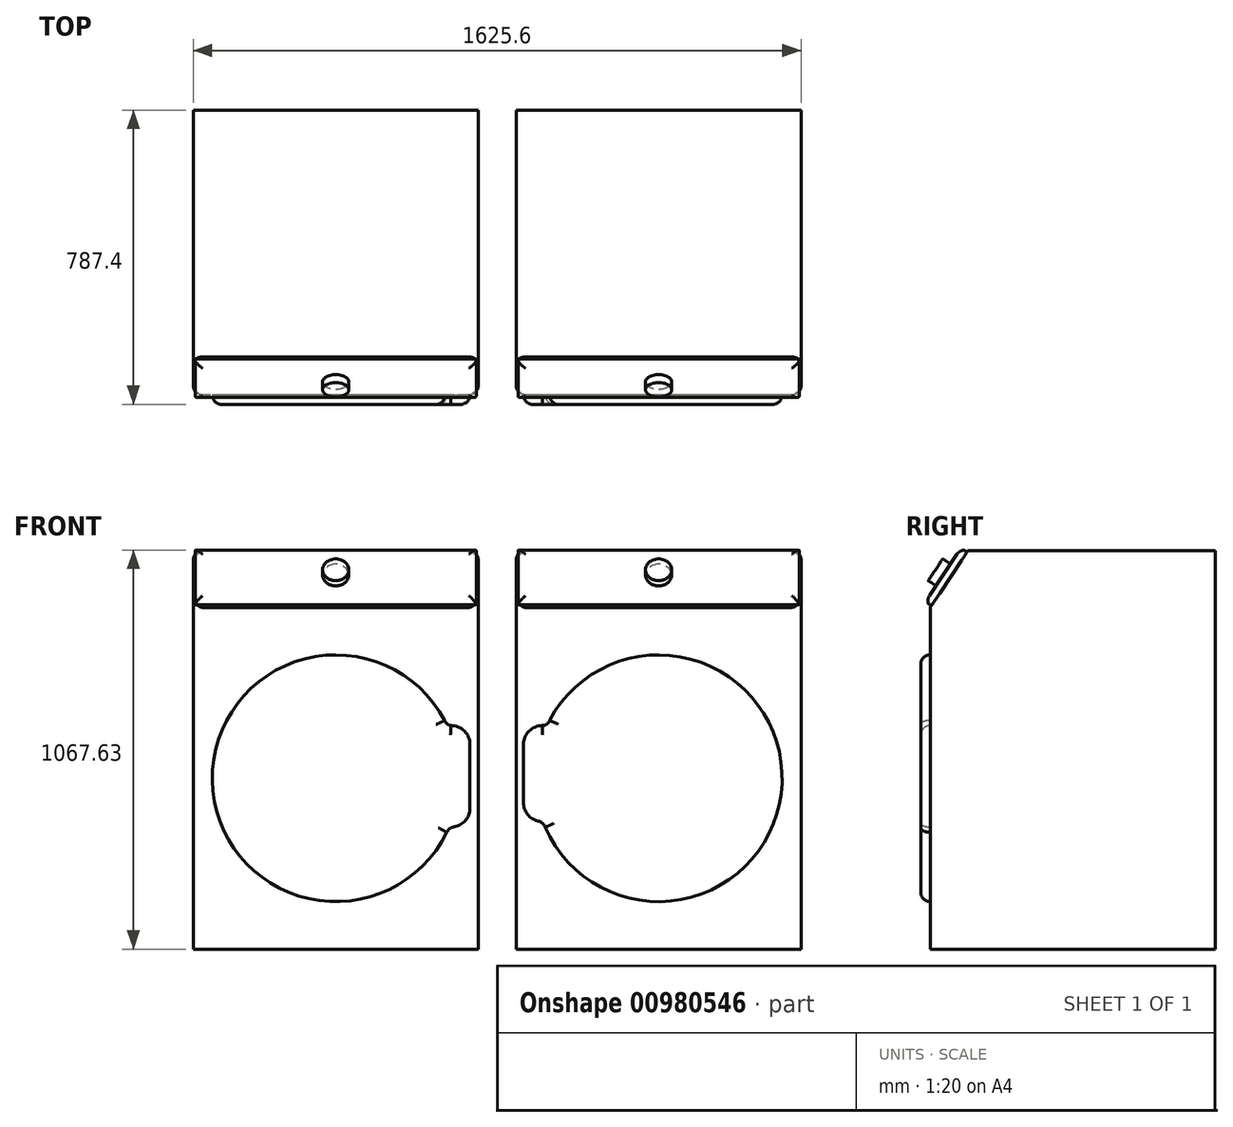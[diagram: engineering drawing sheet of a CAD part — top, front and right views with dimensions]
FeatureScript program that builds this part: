
annotation { "Feature Type Name" : "Feature", "Feature Type Description" : "" }
export const myFeature = defineFeature(function(context is Context, id is Id, definition is map)
    precondition{}
    {
        {
            var Q0;
            Q0=qCreatedBy(makeId("Top.planeOp"),FACE);
            var sketch = newSketch(context, id + "F0", { "sketchPlane" : qUnion([Q0])});
            skLineSegment(sketch, "E0.bottom", {"start": v(-50.8, 381) * mm, "end": v(-812.8, 381) * mm});
            skLineSegment(sketch, "E0.top", {"start": v(-50.8, -381) * mm, "end": v(-812.8, -381) * mm});
            skLineSegment(sketch, "E0.left", {"start": v(-50.8, 381) * mm, "end": v(-50.8, -381) * mm});
            skLineSegment(sketch, "E0.right", {"start": v(-812.8, 381) * mm, "end": v(-812.8, -381) * mm});
            skPoint(sketch, "E0.middle", {"position": v(-431.8, 0) * mm});
            skLineSegment(sketch, "E1.bottom", {"start": v(812.8, 381) * mm, "end": v(50.8, 381) * mm});
            skLineSegment(sketch, "E1.top", {"start": v(812.8, -381) * mm, "end": v(50.8, -381) * mm});
            skLineSegment(sketch, "E1.left", {"start": v(812.8, 381) * mm, "end": v(812.8, -381) * mm});
            skLineSegment(sketch, "E1.right", {"start": v(50.8, 381) * mm, "end": v(50.8, -381) * mm});
            skPoint(sketch, "E1.middle", {"position": v(431.8, 0) * mm});
            skLineSegment(sketch, "E2", {"start": v(-431.8, 0) * mm, "end": v(420.9, 0) * mm, "construction": true});
            skSolve(sketch);
        }
        {
            var Q0;
            Q0=makeQuery(id+"F0.imprint","IMPRINT",FACE,{"disambiguationData":[TD([[makeQuery(id+"F0.imprint","IMPRINT",EDGE,{"derivedFrom":sQuery(id+"F0.wireOp",EDGE,"E0.bottom")}),1.0]])]});
            var Q1;
            Q1=makeQuery(id+"F0.imprint","IMPRINT",FACE,{"disambiguationData":[TD([[makeQuery(id+"F0.imprint","IMPRINT",EDGE,{"derivedFrom":sQuery(id+"F0.wireOp",EDGE,"E1.bottom")}),1.0]])]});
            extrude(context, id + "F1", {"entities" : qUnion([Q0, Q1]), "depth" : 1066.8 * mm, "offsetDistance" : 25.4 * mm});
        }
        {
            var Q0;
            Q0=makeQuery(id+"F1.opExtrude","CAP_EDGE",EDGE,{"disambiguationData":[OSD([sQuery(id+"F0.wireOp",EDGE,"E0.top")])],"isStart":false});
            var Q1;
            Q1=makeQuery(id+"F1.opExtrude","CAP_EDGE",EDGE,{"disambiguationData":[OSD([sQuery(id+"F0.wireOp",EDGE,"E1.top")])],"isStart":false});
            chamfer(context, id + "F2", {"entities" : qUnion([Q0, Q1]), "chamferType" : ChamferType.TWO_OFFSETS, "width1" : 152.4 * mm, "oppositeDirection" : false, "width2" : 101.6 * mm, "tangentPropagation" : true});
        }
        {
            var Q0;
            Q0=makeQuery(id+"F2.opChamfer","BLEND_FACE",FACE,{"disambiguationData":[OSD([sQuery(id+"F0.wireOp",EDGE,"E0.top")])]});
            var Q1;
            Q1=makeQuery(id+"F2.opChamfer","BLEND_FACE",FACE,{"disambiguationData":[OSD([sQuery(id+"F0.wireOp",EDGE,"E1.top")])]});
            extrude(context, id + "F3", {"entities" : qUnion([Q0, Q1]), "depth" : 19.05 * mm, "offsetDistance" : 25.4 * mm});
        }
        {
            var Q0;
            Q0=makeQuery(id+"F1.opExtrude","SWEPT_FACE",FACE,{"disambiguationData":[OSD([sQuery(id+"F0.wireOp",EDGE,"E0.top")])]});
            var sketch = newSketch(context, id + "F4", { "sketchPlane" : qUnion([Q0])});
            skLineSegment(sketch, "E3", {"start": v(-50.8, 457.2) * mm, "end": v(-812.8, 457.2) * mm, "construction": true});
            skArc(sketch, "E4", {"start": v(-140.06, 611.86) * mm, "mid": v(-761.95, 451.64) * mm, "end": v(-135.01, 312.46) * mm});
            skLineSegment(sketch, "E5", {"start": v(-50.8, 457.2) * mm, "end": v(50.8, 457.2) * mm, "construction": true});
            skLineSegment(sketch, "E6", {"start": v(50.8, 457.2) * mm, "end": v(812.8, 457.2) * mm, "construction": true});
            skArc(sketch, "E7", {"start": v(128.77, 326.03) * mm, "mid": v(761.74, 444.17) * mm, "end": v(140.06, 611.86) * mm});
            skLineSegment(sketch, "E8.right", {"start": v(-72.72, 377.53) * mm, "end": v(-72.72, 547.55) * mm});
            skLineSegment(sketch, "E9.right", {"start": v(70.34, 392.14) * mm, "end": v(70.34, 547.55) * mm});
            skPoint(sketch, "E10.visualSharp", {"position": v(-72.72, 598.35) * mm});
            skArc(sketch, "E10.filletArc", {"start": v(-72.72, 547.55) * mm, "mid": v(-87.6, 583.48) * mm, "end": v(-123.52, 598.35) * mm});
            skPoint(sketch, "E11.visualSharp", {"position": v(-72.72, 326.73) * mm});
            skArc(sketch, "E11.filletArc", {"start": v(-115.37, 327.39) * mm, "mid": v(-84.83, 344.61) * mm, "end": v(-72.72, 377.53) * mm});
            skPoint(sketch, "E12.visualSharp", {"position": v(70.34, 341.34) * mm});
            skArc(sketch, "E12.filletArc", {"start": v(70.34, 392.14) * mm, "mid": v(81.5, 360.38) * mm, "end": v(110.05, 342.57) * mm});
            skPoint(sketch, "E13.visualSharp", {"position": v(70.34, 598.35) * mm});
            skArc(sketch, "E13.filletArc", {"start": v(121.14, 598.35) * mm, "mid": v(85.22, 583.48) * mm, "end": v(70.34, 547.55) * mm});
            skLineSegment(sketch, "E14", {"start": v(-133.3, 598.35) * mm, "end": v(-72.72, 462.54) * mm, "construction": true});
            skLineSegment(sketch, "E15", {"start": v(70.34, 471.33) * mm, "end": v(133.3, 598.35) * mm, "construction": true});
            skPoint(sketch, "E16.visualSharp", {"position": v(-133.3, 598.35) * mm});
            skPoint(sketch, "E17.visualSharp", {"position": v(133.3, 598.35) * mm});
            skPoint(sketch, "E18.visualSharp", {"position": v(122.6, 341.34) * mm});
            skLineSegment(sketch, "E19", {"start": v(127.24, 329.1) * mm, "end": v(128.77, 326.03) * mm});
            skPoint(sketch, "E20.visualSharp", {"position": v(121.14, 341.34) * mm});
            skArc(sketch, "E20.filletArc", {"start": v(127.24, 329.1) * mm, "mid": v(120.16, 337.78) * mm, "end": v(110.05, 342.57) * mm});
            skPoint(sketch, "E21.visualSharp", {"position": v(-128.47, 326.73) * mm});
            skLineSegment(sketch, "E22", {"start": v(-135.01, 312.46) * mm, "end": v(-132.54, 316.23) * mm});
            skPoint(sketch, "E23.visualSharp", {"position": v(-125.64, 326.77) * mm});
            skArc(sketch, "E23.filletArc", {"start": v(-115.37, 327.39) * mm, "mid": v(-125.13, 323.62) * mm, "end": v(-132.54, 316.23) * mm});
            skArc(sketch, "E24", {"start": v(-140.06, 611.86) * mm, "mid": v(-133.62, 602.87) * mm, "end": v(-123.52, 598.35) * mm});
            skArc(sketch, "E25", {"start": v(121.14, 598.35) * mm, "mid": v(133.02, 601.71) * mm, "end": v(140.06, 611.86) * mm});
            skSolve(sketch);
        }
        {
            var Q0;
            Q0=makeQuery(id+"F4.imprint","IMPRINT",FACE,{"disambiguationData":[TD([[makeQuery(id+"F4.imprint","IMPRINT",EDGE,{"derivedFrom":sQuery(id+"F4.wireOp",EDGE,"E4")}),1.0]])]});
            var Q1;
            Q1=makeQuery(id+"F4.imprint","IMPRINT",FACE,{"disambiguationData":[TD([[makeQuery(id+"F4.imprint","IMPRINT",EDGE,{"derivedFrom":sQuery(id+"F4.wireOp",EDGE,"E7")}),1.0]])]});
            extrude(context, id + "F5", {"entities" : qUnion([Q0, Q1]), "depth" : 25.4 * mm, "offsetDistance" : 25.4 * mm});
        }
        {
            var Q0;
            Q0=makeQuery(id+"F3.opExtrude","CAP_FACE",FACE,{"disambiguationData":[OSD([sQuery(id+"F0.wireOp",EDGE,"E1.top")])],"isStart":false});
            var sketch = newSketch(context, id + "F6", { "sketchPlane" : qUnion([Q0])});
            skLineSegment(sketch, "E26", {"start": v(-812.8, 641.07) * mm, "end": v(-50.8, 641.07) * mm, "construction": true});
            skCircle(sketch, "E27", {"center": v(-431.8, 641.07) * mm, "radius": 34.93 * mm});
            skLineSegment(sketch, "E28", {"start": v(50.8, 641.07) * mm, "end": v(812.8, 641.07) * mm, "construction": true});
            skCircle(sketch, "E29", {"center": v(431.8, 641.07) * mm, "radius": 34.93 * mm});
            skSolve(sketch);
        }
        {
            var Q0;
            Q0=makeQuery(id+"F6.imprint","IMPRINT",FACE,{"disambiguationData":[TD([[makeQuery(id+"F6.imprint","IMPRINT",EDGE,{"derivedFrom":sQuery(id+"F6.wireOp",EDGE,"E27")}),1.0]])]});
            var Q1;
            Q1=makeQuery(id+"F6.imprint","IMPRINT",FACE,{"disambiguationData":[TD([[makeQuery(id+"F6.imprint","IMPRINT",EDGE,{"derivedFrom":sQuery(id+"F6.wireOp",EDGE,"E29")}),1.0]])]});
            extrude(context, id + "F7", {"entities" : qUnion([Q0, Q1]), "depth" : 25.4 * mm, "offsetDistance" : 25.4 * mm});
        }
        {
            var Q0;
            Q0=makeQuery(id+"F5.opExtrude","CAP_EDGE",EDGE,{"disambiguationData":[OSD([sQuery(id+"F4.wireOp",EDGE,"E4")])],"isStart":false});
            var Q1;
            Q1=makeQuery(id+"F5.opExtrude","CAP_EDGE",EDGE,{"disambiguationData":[OSD([sQuery(id+"F4.wireOp",EDGE,"E10.filletArc")])],"isStart":false});
            var Q2;
            Q2=makeQuery(id+"F5.opExtrude","CAP_EDGE",EDGE,{"disambiguationData":[OSD([sQuery(id+"F4.wireOp",EDGE,"E24")])],"isStart":false});
            var Q3;
            Q3=makeQuery(id+"F5.opExtrude","CAP_EDGE",EDGE,{"disambiguationData":[OSD([sQuery(id+"F4.wireOp",EDGE,"E12.filletArc")])],"isStart":false});
            var Q4;
            Q4=makeQuery(id+"F5.opExtrude","CAP_EDGE",EDGE,{"disambiguationData":[OSD([sQuery(id+"F4.wireOp",EDGE,"E20.filletArc")])],"isStart":false});
            var Q5;
            Q5=makeQuery(id+"F5.opExtrude","CAP_EDGE",EDGE,{"disambiguationData":[OSD([sQuery(id+"F4.wireOp",EDGE,"E7")])],"isStart":false});
            var Q6;
            Q6=makeQuery(id+"F5.opExtrude","CAP_EDGE",EDGE,{"disambiguationData":[OSD([sQuery(id+"F4.wireOp",EDGE,"E19")])],"isStart":false});
            var Q7;
            Q7=makeQuery(id+"F5.opExtrude","CAP_EDGE",EDGE,{"disambiguationData":[OSD([sQuery(id+"F4.wireOp",EDGE,"E9.right")])],"isStart":false});
            var Q8;
            Q8=makeQuery(id+"F5.opExtrude","CAP_EDGE",EDGE,{"disambiguationData":[OSD([sQuery(id+"F4.wireOp",EDGE,"E25")])],"isStart":false});
            var Q9;
            Q9=makeQuery(id+"F3.opExtrude","CAP_EDGE",EDGE,{"disambiguationData":[OSD([sQuery(id+"F0.wireOp",EDGE,"E0.bottom"),sQuery(id+"F0.wireOp",EDGE,"E0.top"),sQuery(id+"F0.wireOp",EDGE,"E0.left"),sQuery(id+"F0.wireOp",EDGE,"E0.right")])],"isStart":false});
            var Q10;
            Q10=makeQuery(id+"F3.opExtrude","CAP_EDGE",EDGE,{"disambiguationData":[OSD([sQuery(id+"F0.wireOp",EDGE,"E0.top"),sQuery(id+"F0.wireOp",EDGE,"E0.left")])],"isStart":false});
            var Q11;
            Q11=makeQuery(id+"F3.opExtrude","CAP_EDGE",EDGE,{"disambiguationData":[OSD([sQuery(id+"F0.wireOp",EDGE,"E0.top")])],"isStart":false});
            var Q12;
            Q12=makeQuery(id+"F3.opExtrude","CAP_EDGE",EDGE,{"disambiguationData":[OSD([sQuery(id+"F0.wireOp",EDGE,"E0.top"),sQuery(id+"F0.wireOp",EDGE,"E0.right")])],"isStart":false});
            var Q13;
            Q13=makeQuery(id+"F3.opExtrude","CAP_EDGE",EDGE,{"disambiguationData":[OSD([sQuery(id+"F0.wireOp",EDGE,"E1.top"),sQuery(id+"F0.wireOp",EDGE,"E1.right")])],"isStart":false});
            var Q14;
            Q14=makeQuery(id+"F3.opExtrude","CAP_EDGE",EDGE,{"disambiguationData":[OSD([sQuery(id+"F0.wireOp",EDGE,"E1.bottom"),sQuery(id+"F0.wireOp",EDGE,"E1.top"),sQuery(id+"F0.wireOp",EDGE,"E1.left"),sQuery(id+"F0.wireOp",EDGE,"E1.right")])],"isStart":false});
            var Q15;
            Q15=makeQuery(id+"F3.opExtrude","CAP_EDGE",EDGE,{"disambiguationData":[OSD([sQuery(id+"F0.wireOp",EDGE,"E1.top")])],"isStart":false});
            var Q16;
            Q16=makeQuery(id+"F3.opExtrude","CAP_EDGE",EDGE,{"disambiguationData":[OSD([sQuery(id+"F0.wireOp",EDGE,"E1.top"),sQuery(id+"F0.wireOp",EDGE,"E1.left")])],"isStart":false});
            var Q17;
            Q17=makeQuery(id+"F1.opExtrude","SWEPT_EDGE",EDGE,{"disambiguationData":[OSD([sQuery(id+"F0.wireOp",EDGE,"E1.top"),sQuery(id+"F0.wireOp",EDGE,"E1.right")])]});
            var Q18;
            Q18=makeQuery(id+"F1.opExtrude","SWEPT_EDGE",EDGE,{"disambiguationData":[OSD([sQuery(id+"F0.wireOp",EDGE,"E0.top"),sQuery(id+"F0.wireOp",EDGE,"E0.left")])]});
            var Q19;
            Q19=makeQuery(id+"F1.opExtrude","SWEPT_EDGE",EDGE,{"disambiguationData":[OSD([sQuery(id+"F0.wireOp",EDGE,"E0.top"),sQuery(id+"F0.wireOp",EDGE,"E0.right")])]});
            var Q20;
            Q20=makeQuery(id+"F1.opExtrude","SWEPT_EDGE",EDGE,{"disambiguationData":[OSD([sQuery(id+"F0.wireOp",EDGE,"E1.top"),sQuery(id+"F0.wireOp",EDGE,"E1.left")])]});
            var Q21;
            Q21=makeQuery(id+"F1.opExtrude","CAP_EDGE",EDGE,{"disambiguationData":[OSD([sQuery(id+"F0.wireOp",EDGE,"E1.left")])],"isStart":false});
            var Q22;
            Q22=makeQuery(id+"F1.opExtrude","CAP_EDGE",EDGE,{"disambiguationData":[OSD([sQuery(id+"F0.wireOp",EDGE,"E1.right")])],"isStart":false});
            var Q23;
            Q23=makeQuery(id+"F1.opExtrude","CAP_EDGE",EDGE,{"disambiguationData":[OSD([sQuery(id+"F0.wireOp",EDGE,"E0.left")])],"isStart":false});
            var Q24;
            Q24=makeQuery(id+"F1.opExtrude","CAP_EDGE",EDGE,{"disambiguationData":[OSD([sQuery(id+"F0.wireOp",EDGE,"E0.right")])],"isStart":false});
            fillet(context, id + "F8", {"entities" : qUnion([Q0, Q1, Q2, Q3, Q4, Q5, Q6, Q7, Q8, Q9, Q10, Q11, Q12, Q13, Q14, Q15, Q16, Q17, Q18, Q19, Q20, Q21, Q22, Q23, Q24]), "radius" : 25.4 * mm, "tangentPropagation" : true, "allowEdgeOverflow" : false});
        }
        {
            var Q0;
            {var subQ0=sQuery(id+"F0.wireOp",EDGE,"E1.top");Q0=makeQuery(id+"F8.opFillet","BLEND_EDGE",EDGE,{"blendedFrom":[makeQuery(id+"F3.opExtrude","CAP_EDGE",EDGE,{"disambiguationData":[OSD([subQ0,sQuery(id+"F0.wireOp",EDGE,"E1.left")])],"isStart":false}),makeQuery(id+"F3.opExtrude","CAP_FACE",FACE,{"disambiguationData":[OSD([subQ0])],"isStart":true})],"blendedInto":[makeQuery(id+"F3.opExtrude","CAP_FACE",FACE,{"disambiguationData":[OSD([subQ0])],"isStart":true})]});}
            var Q1;
            {var subQ0=sQuery(id+"F0.wireOp",EDGE,"E1.top");Q1=makeQuery(id+"F8.opFillet","BLEND_EDGE",EDGE,{"blendedFrom":[makeQuery(id+"F3.opExtrude","CAP_EDGE",EDGE,{"disambiguationData":[OSD([subQ0])],"isStart":false}),makeQuery(id+"F3.opExtrude","CAP_FACE",FACE,{"disambiguationData":[OSD([subQ0])],"isStart":true})],"blendedInto":[makeQuery(id+"F3.opExtrude","CAP_FACE",FACE,{"disambiguationData":[OSD([subQ0])],"isStart":true})]});}
            var Q2;
            {var subQ0=sQuery(id+"F0.wireOp",EDGE,"E1.top");Q2=makeQuery(id+"F8.opFillet","BLEND_EDGE",EDGE,{"blendedFrom":[makeQuery(id+"F3.opExtrude","CAP_EDGE",EDGE,{"disambiguationData":[OSD([sQuery(id+"F0.wireOp",EDGE,"E1.bottom"),subQ0,sQuery(id+"F0.wireOp",EDGE,"E1.left"),sQuery(id+"F0.wireOp",EDGE,"E1.right")])],"isStart":false}),makeQuery(id+"F3.opExtrude","CAP_FACE",FACE,{"disambiguationData":[OSD([subQ0])],"isStart":true})],"blendedInto":[makeQuery(id+"F3.opExtrude","CAP_FACE",FACE,{"disambiguationData":[OSD([subQ0])],"isStart":true})]});}
            var Q3;
            {var subQ0=sQuery(id+"F0.wireOp",EDGE,"E1.top");Q3=makeQuery(id+"F8.opFillet","BLEND_EDGE",EDGE,{"blendedFrom":[makeQuery(id+"F3.opExtrude","CAP_EDGE",EDGE,{"disambiguationData":[OSD([subQ0,sQuery(id+"F0.wireOp",EDGE,"E1.right")])],"isStart":false}),makeQuery(id+"F3.opExtrude","CAP_FACE",FACE,{"disambiguationData":[OSD([subQ0])],"isStart":true})],"blendedInto":[makeQuery(id+"F3.opExtrude","CAP_FACE",FACE,{"disambiguationData":[OSD([subQ0])],"isStart":true})]});}
            var Q4;
            {var subQ0=sQuery(id+"F0.wireOp",EDGE,"E0.top");Q4=makeQuery(id+"F8.opFillet","BLEND_EDGE",EDGE,{"blendedFrom":[makeQuery(id+"F3.opExtrude","CAP_EDGE",EDGE,{"disambiguationData":[OSD([sQuery(id+"F0.wireOp",EDGE,"E0.bottom"),subQ0,sQuery(id+"F0.wireOp",EDGE,"E0.left"),sQuery(id+"F0.wireOp",EDGE,"E0.right")])],"isStart":false}),makeQuery(id+"F3.opExtrude","CAP_FACE",FACE,{"disambiguationData":[OSD([subQ0])],"isStart":true})],"blendedInto":[makeQuery(id+"F3.opExtrude","CAP_FACE",FACE,{"disambiguationData":[OSD([subQ0])],"isStart":true})]});}
            var Q5;
            {var subQ0=sQuery(id+"F0.wireOp",EDGE,"E0.top");Q5=makeQuery(id+"F8.opFillet","BLEND_EDGE",EDGE,{"blendedFrom":[makeQuery(id+"F3.opExtrude","CAP_EDGE",EDGE,{"disambiguationData":[OSD([subQ0,sQuery(id+"F0.wireOp",EDGE,"E0.left")])],"isStart":false}),makeQuery(id+"F3.opExtrude","CAP_FACE",FACE,{"disambiguationData":[OSD([subQ0])],"isStart":true})],"blendedInto":[makeQuery(id+"F3.opExtrude","CAP_FACE",FACE,{"disambiguationData":[OSD([subQ0])],"isStart":true})]});}
            var Q6;
            {var subQ0=sQuery(id+"F0.wireOp",EDGE,"E0.top");Q6=makeQuery(id+"F8.opFillet","BLEND_EDGE",EDGE,{"blendedFrom":[makeQuery(id+"F3.opExtrude","CAP_EDGE",EDGE,{"disambiguationData":[OSD([subQ0])],"isStart":false}),makeQuery(id+"F3.opExtrude","CAP_FACE",FACE,{"disambiguationData":[OSD([subQ0])],"isStart":true})],"blendedInto":[makeQuery(id+"F3.opExtrude","CAP_FACE",FACE,{"disambiguationData":[OSD([subQ0])],"isStart":true})]});}
            var Q7;
            {var subQ0=sQuery(id+"F0.wireOp",EDGE,"E0.top");Q7=makeQuery(id+"F8.opFillet","BLEND_EDGE",EDGE,{"blendedFrom":[makeQuery(id+"F3.opExtrude","CAP_EDGE",EDGE,{"disambiguationData":[OSD([subQ0,sQuery(id+"F0.wireOp",EDGE,"E0.right")])],"isStart":false}),makeQuery(id+"F3.opExtrude","CAP_FACE",FACE,{"disambiguationData":[OSD([subQ0])],"isStart":true})],"blendedInto":[makeQuery(id+"F3.opExtrude","CAP_FACE",FACE,{"disambiguationData":[OSD([subQ0])],"isStart":true})]});}
            fillet(context, id + "F9", {"entities" : qUnion([Q0, Q1, Q2, Q3, Q4, Q5, Q6, Q7]), "radius" : 7.22 * mm, "tangentPropagation" : true, "allowEdgeOverflow" : false});
        }
    });
